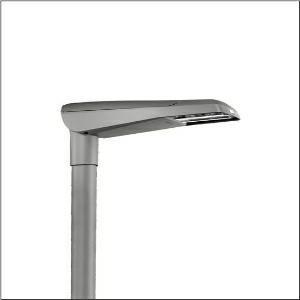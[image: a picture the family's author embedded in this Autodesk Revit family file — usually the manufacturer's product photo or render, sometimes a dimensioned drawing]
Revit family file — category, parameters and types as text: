
# Revit family: streetlight_sl_11_iq_micro___st1_0a_5xc1m41f08ce_367f
name_source: partatom
category: Lighting Fixtures
units: mm (PartAtom-declared; Revit-internal decimal feet)

## family parameters
Cut with Voids When Loaded = No
Host = Face
Light Source = No
Part Type = Normal
Room Calculation Point = No
Round Connector Dimension = Use Diameter
Shared = No

## types (1)
- --- (1 x LED, 1890 lm, 12.6 W, 4000K)
    Apparent Load = 13 VA
    CIE Flux Codes = 33 66 96 100 100
    Color Rendering = 70
    Color Temperature = 4000K
    Default Elevation = 1800 mm
    Description = Streetlight SL 11 iQ micro, mast luminaire, primary light control with 3 zone facetted reflector, of plastic, silver coated, highly specular, primary optical cover: cover, of PMMA, transparent, light distribution: ST1.0a, light emission: direct distribution, primary light characteristic: asymmetric, installation type: post-top, side-entry, lamps: LED, High Power LED, rated values: 1.890lm | 12,6W | 150lm/W (begin service life); end service life: 1.890lm | 12,9W; at 50% lumin. flux: 945lm | 6,8W | 139lm/W, colour temperature: 4000K, colour rendering: CRI > 70, light colour: 740, light setting 1 begin service life: 100% | 1.890lm | 12,6W | 150lm/W | 4.000K, light setting 1 end service life: 12,9W, further light settings possible, control: optimised constant luminous flux control (CLO 2.0), Desk-Remote (wireless, voltage-free reading and setting of iQ features in the workshop via application-optimized NFC function/RFID function), Light-Fading, Smart-Wire, Night-Set, Lumen-Switch, Temp-Guard, Auto-Match, Street-Remote, with cable H07RN-F 5x 1.5mm², mains connection: 230..240V, AC, 50/60Hz, connection cable pre-assembled, cable length: 5,5m, luminaire housing, of diecast aluminium, powder-coated, Siteco® metallic grey (DB 702S), please order mast flange separately, inclination adjustable without tools: 0°, 5°, 10°, 15° (post-top) | 0°, -5°, -10°, -15° (side-entry), sealing non-destructively replaceable, multi-level sealing system, length: 600mm, width: 174mm, height: 116mm, mast flange for spigot size: 42mm (side-entry): 5XC10008XM4, 60/48mm (side-entry/post-top): 5XC10108XM2, 76/60mm (side-entry/post-top): 5XC10108XM1, equipment: standard, protection rating (complete): IP66, insulation class (complete): insulation class II (safety insulation), certification: CE, ENEC, ENEC+, VDE, impact resistance: IK10, permissible operating ambient temperature for outdoor applications: -25..+50°C, standard-compliant lighting for roads and squares, Environmental Product Declaration (EPD) tested and certified by an independent institute, packaging unit: 1 piece

Light Distribution: ST1.0a
    Height = 116 mm
    Lamp = 1 x LED
    Lamp Light Flux = 1890 lm
    Lamp Power = 12.6 W
    Lamp count = 1
    Length = 600 mm
    Luminous efficacy = 150 lm/W
    Manufacturer = Siteco
    ModVariant = No
    Model = 5XC1M41F08CE
    Number of Poles = 1
    OnlyDefault = Yes
    Power Factor = 1
    Product Name = Streetlight SL 11 iQ micro | ST1.0a
    Product group = mast luminaire | pylon top
    ProductGroupID = 6100
    Protection Class = Protection class II
    Protection Degree = IP 66
    RLX_Detail_Level = 1
    RLX_Emergency_Light_Flux = 0 lm
    RLX_Emergency_Type = 0
    RLX_Emergency_Type_DB = No
    RlxData = <blob elided: 26261 chars, md5=e1ad13b8>
    Socket = socket
    Standby Power = 0 W
    System Light Flux = 1890 lm
    System Power = 13 W
    Type Comments = factory setting: luminous flux: 100 % | dim-lin: 254 | 229 mA
    Type Image = l_1006566.jpg
    URL = http://relux.com
    VarID = @adj_020499
    Voltage = 0 V
    Weight = 0.00 kg
    Width = 174 mm

## geometry (parser evidence)
native form markers: Blend x4, Sweep x13
no freeform markers — native parametric forms only
